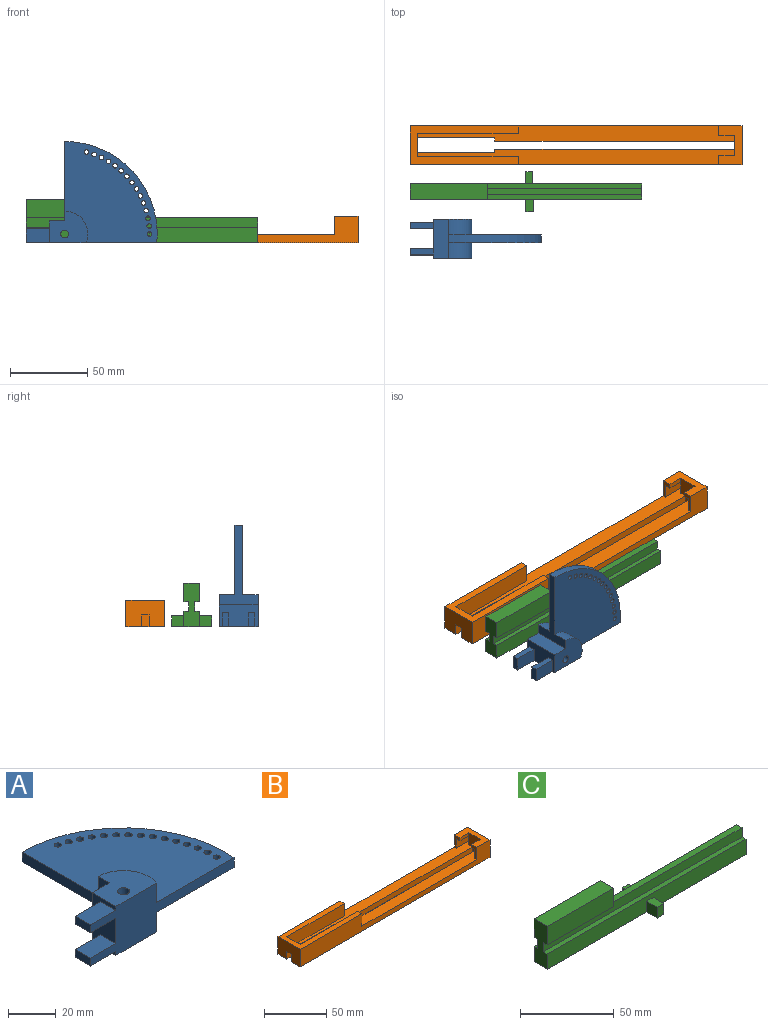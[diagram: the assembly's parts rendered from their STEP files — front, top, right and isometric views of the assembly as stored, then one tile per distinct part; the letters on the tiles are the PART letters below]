
ASSEMBLY  parts=3 mates=4
PART A: 35 faces, bbox 85x65.5x25 mm
  f0: plane 51.5x25mm, normal (-1,0,0), area 387.5mm2, adj f16,f17,f18,f22,f31,f32,f33,f34
  f1: cylinder r=1.5mm len=5mm, axis (0,0,-1), area 47.1mm2, adj f32,f34
  f2: cylinder r=1.5mm len=5mm, axis (0,0,-1), area 47.1mm2, adj f32,f34
  f3: cylinder r=1.5mm len=5mm, axis (0,0,-1), area 47.1mm2, adj f32,f34
  f4: cylinder r=1.5mm len=5mm, axis (0,0,-1), area 47.1mm2, adj f32,f34
  f5: cylinder r=1.5mm len=5mm, axis (0,0,-1), area 47.1mm2, adj f32,f34
  f6: cylinder r=1.5mm len=5mm, axis (0,0,-1), area 47.1mm2, adj f32,f34
  f7: cylinder r=1.5mm len=5mm, axis (0,0,-1), area 47.1mm2, adj f32,f34
  f8: cylinder r=1.5mm len=5mm, axis (0,0,-1), area 47.1mm2, adj f32,f34
  f9: cylinder r=1.5mm len=5mm, axis (0,0,-1), area 47.1mm2, adj f32,f34
  f10: cylinder r=1.5mm len=5mm, axis (0,0,-1), area 47.1mm2, adj f32,f34
  f11: cylinder r=1.5mm len=5mm, axis (0,0,-1), area 47.1mm2, adj f32,f34
  f12: cylinder r=1.5mm len=5mm, axis (0,0,-1), area 47.1mm2, adj f32,f34
  f13: cylinder r=1.5mm len=5mm, axis (0,0,-1), area 47.1mm2, adj f32,f34
  f14: cylinder r=1.5mm len=5mm, axis (0,0,-1), area 47.1mm2, adj f32,f34
  f15: cylinder r=1.5mm len=5mm, axis (0,0,-1), area 47.1mm2, adj f32,f34
  f16: cylinder r=60mm len=65.5mm, axis (0,0,-1), area 498.8mm2, adj f0,f20,f32,f34
  f17: plane 25x20.5mm, normal (0,0,1), area 377.7mm2, adj f0,f18,f19,f20,f21,f31
  f18: plane 25x10mm, normal (0,1,0), area 250mm2, adj f0,f17,f19,f22
  f19: plane 25x14mm, normal (-1,0,0), area 278mm2, adj f17,f18,f20,f22,f23,f24,f25,f27
  f20: plane 84.75x25mm, normal (0,-1,0), area 947.8mm2, adj f16,f17,f19,f22,f23,f25,f26,f27
  f21: cylinder r=2.5mm len=25mm, axis (0,0,-1), area 392.7mm2, adj f17,f22
  f22: plane 25x20.5mm, normal (0,0,-1), area 377.7mm2, adj f0,f18,f19,f20,f21,f33
  f23: plane 15x9mm, normal (0,0,1), area 135mm2, adj f19,f20,f24,f26
  f24: plane 15x4mm, normal (0,1,0), area 60mm2, adj f19,f23,f25,f26
  f25: plane 15x9mm, normal (0,0,-1), area 135mm2, adj f19,f20,f24,f26
  f26: plane 9x4mm, normal (-1,0,0), area 36mm2, adj f20,f23,f24,f25
  f27: plane 15x9mm, normal (0,0,1), area 135mm2, adj f19,f20,f28,f30
  f28: plane 15x4mm, normal (0,1,0), area 60mm2, adj f19,f27,f29,f30
  f29: plane 15x9mm, normal (0,0,-1), area 135mm2, adj f19,f20,f28,f30
  f30: plane 9x4mm, normal (-1,0,0), area 36mm2, adj f20,f27,f28,f29
  f31: cylinder r=15mm len=20.5mm, axis (0,0,1), area 291.9mm2, adj f0,f17,f20,f32
  f32: plane 65.5x60mm, normal (0,0,1), area 2793.6mm2, adj f0,f1,f2,f3,f4,f5,f6,f7
  f33: cylinder r=15mm len=20.5mm, axis (0,0,-1), area 291.9mm2, adj f0,f20,f22,f34
  f34: plane 65.5x60mm, normal (0,0,-1), area 2793.6mm2, adj f0,f1,f2,f3,f4,f5,f6,f7
PART B: 34 faces, bbox 215x25x17 mm
  f0: plane 10x3mm, normal (0,-1,0), area 30mm2, adj f3,f13,f27,f29
  f1: plane 25x17mm, normal (1,0,0), area 353mm2, adj f4,f5,f6,f18,f19,f27,f28,f29
  f2: plane 12x6mm, normal (-1,0,0), area 36mm2, adj f4,f18,f26,f27,f31,f33
  f3: plane 12x6mm, normal (-1,0,0), area 36mm2, adj f0,f5,f6,f27,f29,f30
  f4: plane 210x10mm, normal (0,0,1), area 1600mm2, adj f1,f2,f9,f13,f14,f15,f16,f18
  f5: plane 210x10mm, normal (0,0,1), area 1600mm2, adj f1,f3,f6,f9,f10,f11,f12,f13
  f6: plane 215x17mm, normal (0,1,0), area 2095mm2, adj f1,f3,f5,f7,f19,f23,f24,f27
  f7: plane 25x17mm, normal (-1,0,0), area 387.5mm2, adj f6,f8,f17,f18,f19,f24,f25
  f8: plane 7.5x5mm, normal (0,-1,0), area 37.5mm2, adj f7,f9,f19,f25
  f9: plane 17x15mm, normal (1,0,0), area 192.5mm2, adj f4,f5,f8,f10,f16,f17,f19,f21
  f10: plane 50x5mm, normal (0,-1,0), area 250mm2, adj f5,f9,f11,f19
  f11: plane 5x2.5mm, normal (-1,0,0), area 12.5mm2, adj f5,f10,f12,f19
  f12: plane 155x5mm, normal (0,-1,0), area 775mm2, adj f5,f11,f13,f19
  f13: plane 17x13mm, normal (-1,0,0), area 181mm2, adj f0,f4,f5,f12,f14,f19,f26,f27
  f14: plane 155x5mm, normal (0,1,0), area 775mm2, adj f4,f13,f15,f19
  f15: plane 5x2.5mm, normal (-1,0,0), area 12.5mm2, adj f4,f14,f16,f19
  f16: plane 50x5mm, normal (0,1,0), area 250mm2, adj f4,f9,f15,f19
  f17: plane 7.5x5mm, normal (0,1,0), area 37.5mm2, adj f7,f9,f19,f25
  f18: plane 215x17mm, normal (0,-1,0), area 2095mm2, adj f1,f2,f4,f7,f19,f20,f24,f27
  f19: plane 215x25mm, normal (0,0,-1), area 4075mm2, adj f1,f6,f7,f8,f9,f10,f11,f12
  f20: plane 12x5mm, normal (1,0,0), area 60mm2, adj f4,f18,f21,f24
  f21: plane 65x12mm, normal (0,1,0), area 780mm2, adj f4,f9,f20,f24
  f22: plane 65x12mm, normal (0,-1,0), area 780mm2, adj f5,f9,f23,f24
  f23: plane 12x5mm, normal (1,0,0), area 60mm2, adj f5,f6,f22,f24
  f24: plane 70x25mm, normal (0,0,1), area 775mm2, adj f6,f7,f9,f18,f20,f21,f22,f23
  f25: plane 5x5mm, normal (0,0,-1), area 25mm2, adj f7,f8,f9,f17
  f26: plane 10x3mm, normal (0,1,0), area 30mm2, adj f2,f13,f27,f33
  f27: plane 25x15mm, normal (0,0,1), area 245mm2, adj f0,f1,f2,f3,f6,f13,f18,f26
  f28: plane 9x5mm, normal (0,1,0), area 45mm2, adj f1,f5,f13,f29
  f29: plane 15x4mm, normal (0,0,-1), area 60mm2, adj f0,f1,f3,f28,f30
  f30: plane 15x9mm, normal (0,-1,0), area 135mm2, adj f1,f3,f5,f29
  f31: plane 15x9mm, normal (0,1,0), area 135mm2, adj f1,f2,f4,f33
  f32: plane 9x5mm, normal (0,-1,0), area 45mm2, adj f1,f4,f13,f33
  f33: plane 15x4mm, normal (0,0,-1), area 60mm2, adj f1,f2,f26,f31,f32
PART C: 28 faces, bbox 150x26x28 mm
  f0: plane 150x3mm, normal (0,0,1), area 450mm2, adj f10,f14,f15,f20
  f1: plane 8x5mm, normal (0,0,1), area 40mm2, adj f3,f4,f5,f6
  f2: plane 8x4.49mm, normal (0,0,1), area 35.9mm2, adj f11,f12,f13,f14
  f3: plane 8x7mm, normal (-1,0,0), area 56mm2, adj f1,f4,f6,f16
  f4: plane 7x5mm, normal (0,-1,0), area 35mm2, adj f1,f3,f5,f16
  f5: plane 8x7mm, normal (1,0,0), area 56mm2, adj f1,f4,f6,f16
  f6: plane 150x10mm, normal (0,-1,0), area 1465mm2, adj f1,f3,f5,f10,f15,f16,f18
  f7: plane 148x7mm, normal (0,1,0), area 1036mm2, adj f8,f10,f16,f17
  f8: plane 7x2mm, normal (1,0,0), area 14mm2, adj f7,f9,f16,f17
  f9: plane 148x7mm, normal (0,-1,0), area 1036mm2, adj f8,f10,f16,f17
  f10: plane 16x10mm, normal (1,0,0), area 110mm2, adj f0,f6,f7,f9,f14,f16,f17,f18
  f11: plane 8x7mm, normal (1,0,0), area 56mm2, adj f2,f12,f14,f16
  f12: plane 7x4.49mm, normal (0,1,0), area 31.4mm2, adj f2,f11,f13,f16
  f13: plane 8x7mm, normal (-1,0,0), area 56mm2, adj f2,f12,f14,f16
  f14: plane 150x10mm, normal (0,1,0), area 1468.6mm2, adj f0,f2,f10,f11,f13,f15,f16
  f15: plane 28x10mm, normal (-1,0,0), area 244mm2, adj f0,f6,f14,f16,f18,f19,f20,f22
  f16: plane 150x26mm, normal (0,0,-1), area 1279.9mm2, adj f3,f4,f5,f6,f7,f8,f9,f10
  f17: plane 148x2mm, normal (0,0,-1), area 296mm2, adj f7,f8,f9,f10
  f18: plane 150x3mm, normal (0,0,1), area 450mm2, adj f6,f10,f15,f19
  f19: plane 150x6mm, normal (0,-1,0), area 900mm2, adj f10,f15,f18,f21,f22
  f20: plane 150x6mm, normal (0,1,0), area 900mm2, adj f0,f10,f15,f21,f27
  f21: plane 100x4mm, normal (0,0,1), area 400mm2, adj f10,f19,f20,f23
  f22: plane 50x3mm, normal (0,0,-1), area 150mm2, adj f15,f19,f23,f25
  f23: plane 12x10mm, normal (1,0,0), area 120mm2, adj f21,f22,f24,f25,f26,f27
  f24: plane 50x12mm, normal (0,1,0), area 600mm2, adj f15,f23,f26,f27
  f25: plane 50x12mm, normal (0,-1,0), area 600mm2, adj f15,f22,f23,f26
  f26: plane 50x10mm, normal (0,0,1), area 500mm2, adj f15,f23,f24,f25
  f27: plane 50x3mm, normal (0,0,-1), area 150mm2, adj f15,f20,f23,f24
PLACE A rot(axis=(1,0,0),90deg) t=(25,-60.59,5.5)mm
PLACE B t=(215,0,0)mm
PLACE C t=(150,-37.53,0)mm
MATE planar B.f7 <-> C.f15  axis (-1,0,0) through (0,-15,7.5)mm
MATE planar C.f16 <-> B.f19  axis (0,0,-1) through (2,-41.53,0)mm
MATE planar A.f30 <-> C.f15  axis (-1,0,0) through (0,-66.59,4.5)mm
MATE planar A.f20 <-> C.f16  axis (0,0,-1) through (26.98,-85.59,0)mm
